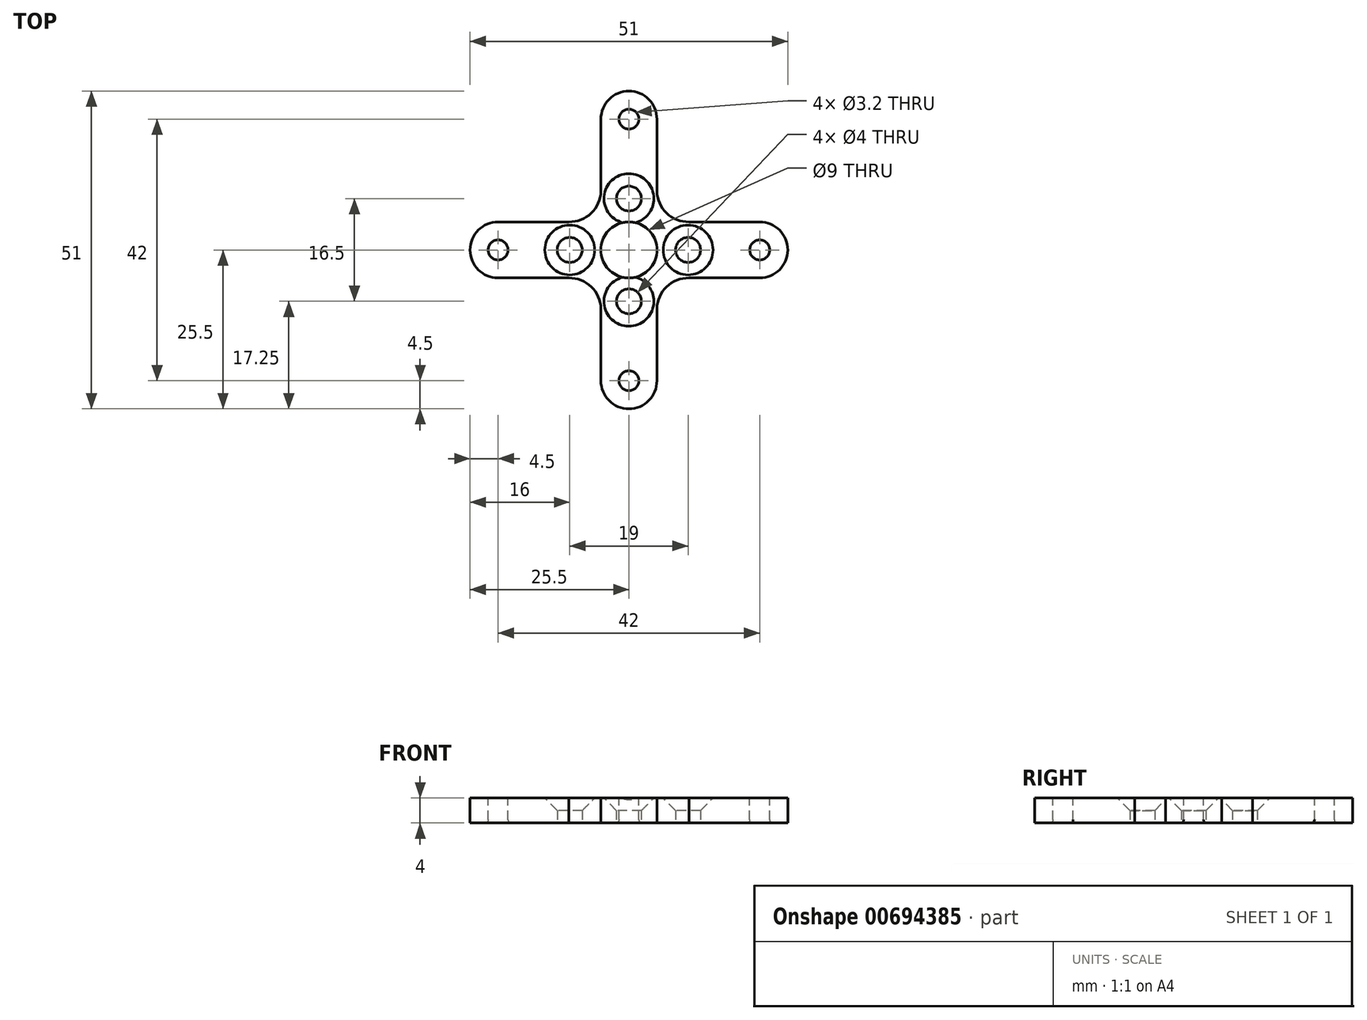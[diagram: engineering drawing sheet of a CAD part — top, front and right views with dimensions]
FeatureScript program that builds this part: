
annotation { "Feature Type Name" : "Feature", "Feature Type Description" : "" }
export const myFeature = defineFeature(function(context is Context, id is Id, definition is map)
    precondition{}
    {
        {
            var Q0;
            Q0=qCreatedBy(makeId("Top.planeOp"),FACE);
            var sketch = newSketch(context, id + "F0", { "sketchPlane" : qUnion([Q0])});
            skLineSegment(sketch, "E0", {"start": v(4.5, -9.46) * mm, "end": v(4.5, -21) * mm});
            skLineSegment(sketch, "E1", {"start": v(9.46, -4.5) * mm, "end": v(21, -4.5) * mm});
            skLineSegment(sketch, "E2.MirrorCS", {"start": v(-4.5, -9.46) * mm, "end": v(-4.5, -21) * mm});
            skLineSegment(sketch, "E3.MirrorCS", {"start": v(9.46, 4.5) * mm, "end": v(21, 4.5) * mm});
            skLineSegment(sketch, "E4.MirrorCS", {"start": v(4.5, 9.46) * mm, "end": v(4.5, 21) * mm});
            skLineSegment(sketch, "E5.MirrorCS", {"start": v(-4.5, 9.46) * mm, "end": v(-4.5, 21) * mm});
            skLineSegment(sketch, "E6.MirrorCS", {"start": v(-9.46, 4.5) * mm, "end": v(-21, 4.5) * mm});
            skLineSegment(sketch, "E7.MirrorCS", {"start": v(-9.46, -4.5) * mm, "end": v(-21, -4.5) * mm});
            skArc(sketch, "E8", {"start": v(21, 4.5) * mm, "mid": v(25.5, 0) * mm, "end": v(21, -4.5) * mm});
            skArc(sketch, "E9", {"start": v(4.5, -21) * mm, "mid": v(0, -25.5) * mm, "end": v(-4.5, -21) * mm});
            skArc(sketch, "E10", {"start": v(-21, -4.5) * mm, "mid": v(-25.5, 0) * mm, "end": v(-21, 4.5) * mm});
            skArc(sketch, "E11", {"start": v(-4.5, 21) * mm, "mid": v(0, 25.5) * mm, "end": v(4.5, 21) * mm});
            skLineSegment(sketch, "E12", {"start": v(0, 0) * mm, "end": v(39.03, 39.03) * mm, "construction": true});
            skLineSegment(sketch, "E13", {"start": v(0, 0) * mm, "end": v(29.48, -29.48) * mm, "construction": true});
            skArc(sketch, "E14", {"start": v(4.5, 9.46) * mm, "mid": v(6.06, 5.9) * mm, "end": v(9.68, 4.5) * mm});
            skArc(sketch, "E15.MirrorCS", {"start": v(-4.5, 9.46) * mm, "mid": v(-6.06, 5.9) * mm, "end": v(-9.68, 4.5) * mm});
            skArc(sketch, "E16.MirrorCS", {"start": v(4.5, -9.46) * mm, "mid": v(6.06, -5.9) * mm, "end": v(9.68, -4.5) * mm});
            skArc(sketch, "E17.MirrorCS", {"start": v(-4.5, -9.46) * mm, "mid": v(-6.06, -5.9) * mm, "end": v(-9.68, -4.5) * mm});
            skSolve(sketch);
        }
        {
            var Q0;
            Q0=makeQuery(id+"F0.imprint","IMPRINT",FACE,{"disambiguationData":[TD([[makeQuery(id+"F0.imprint","IMPRINT",EDGE,{"derivedFrom":sQuery(id+"F0.wireOp",EDGE,"E0")}),-1.0]])]});
            extrude(context, id + "F1", {"entities" : qUnion([Q0]), "depth" : 4 * mm, "offsetDistance" : 25 * mm});
        }
        {
            var Q0;
            Q0=makeQuery(id+"F1.opExtrude","CAP_FACE",FACE,{"disambiguationData":[OSD([sQuery(id+"F0.wireOp",EDGE,"E0"),sQuery(id+"F0.wireOp",EDGE,"E1"),sQuery(id+"F0.wireOp",EDGE,"E2.MirrorCS"),sQuery(id+"F0.wireOp",EDGE,"E3.MirrorCS"),sQuery(id+"F0.wireOp",EDGE,"E4.MirrorCS"),sQuery(id+"F0.wireOp",EDGE,"E5.MirrorCS"),sQuery(id+"F0.wireOp",EDGE,"E6.MirrorCS"),sQuery(id+"F0.wireOp",EDGE,"E7.MirrorCS"),sQuery(id+"F0.wireOp",EDGE,"E8"),sQuery(id+"F0.wireOp",EDGE,"E9"),sQuery(id+"F0.wireOp",EDGE,"E10"),sQuery(id+"F0.wireOp",EDGE,"E11"),sQuery(id+"F0.wireOp",EDGE,"E14"),sQuery(id+"F0.wireOp",EDGE,"E15.MirrorCS"),sQuery(id+"F0.wireOp",EDGE,"E16.MirrorCS"),sQuery(id+"F0.wireOp",EDGE,"E17.MirrorCS")])],"isStart":false});
            var sketch = newSketch(context, id + "F2", { "sketchPlane" : qUnion([Q0])});
            skCircle(sketch, "E18", {"center": v(0, 0) * mm, "radius": 4.5 * mm});
            skSolve(sketch);
        }
        {
            var Q0;
            Q0 = qSketchRegion(id + "F2", true);
            extrude(context, id + "F3", {"entities" : qUnion([Q0]), "operationType" : NewBodyOperationType.REMOVE, "endBound" : BoundingType.THROUGH_ALL, "oppositeDirection" : true, "depth" : 3 * mm, "offsetDistance" : 25 * mm});
        }
        {
            var Q0;
            Q0=makeQuery(id+"F1.opExtrude","CAP_FACE",FACE,{"disambiguationData":[OSD([sQuery(id+"F0.wireOp",EDGE,"E0"),sQuery(id+"F0.wireOp",EDGE,"E1"),sQuery(id+"F0.wireOp",EDGE,"E2.MirrorCS"),sQuery(id+"F0.wireOp",EDGE,"E3.MirrorCS"),sQuery(id+"F0.wireOp",EDGE,"E4.MirrorCS"),sQuery(id+"F0.wireOp",EDGE,"E5.MirrorCS"),sQuery(id+"F0.wireOp",EDGE,"E6.MirrorCS"),sQuery(id+"F0.wireOp",EDGE,"E7.MirrorCS"),sQuery(id+"F0.wireOp",EDGE,"E8"),sQuery(id+"F0.wireOp",EDGE,"E9"),sQuery(id+"F0.wireOp",EDGE,"E10"),sQuery(id+"F0.wireOp",EDGE,"E11"),sQuery(id+"F0.wireOp",EDGE,"E14"),sQuery(id+"F0.wireOp",EDGE,"E15.MirrorCS"),sQuery(id+"F0.wireOp",EDGE,"E16.MirrorCS"),sQuery(id+"F0.wireOp",EDGE,"E17.MirrorCS")])],"isStart":false});
            var sketch = newSketch(context, id + "F4", { "sketchPlane" : qUnion([Q0])});
            skCircle(sketch, "E19", {"center": v(21, 0) * mm, "radius": 1.6 * mm});
            skCircle(sketch, "E20", {"center": v(0, -21) * mm, "radius": 1.6 * mm});
            skCircle(sketch, "E21.MirrorC", {"center": v(-21, 0) * mm, "radius": 1.6 * mm});
            skCircle(sketch, "E22.MirrorC", {"center": v(0, 21) * mm, "radius": 1.6 * mm});
            skSolve(sketch);
        }
        {
            var Q0;
            Q0 = qSketchRegion(id + "F4", true);
            extrude(context, id + "F5", {"entities" : qUnion([Q0]), "operationType" : NewBodyOperationType.REMOVE, "endBound" : BoundingType.THROUGH_ALL, "oppositeDirection" : true, "depth" : 25 * mm, "offsetDistance" : 25 * mm});
        }
        {
            var Q0;
            Q0=qCreatedBy(makeId("Top.planeOp"),FACE);
            var sketch = newSketch(context, id + "F6", { "sketchPlane" : qUnion([Q0])});
            skCircle(sketch, "E23", {"center": v(9.5, 0) * mm, "radius": 2 * mm});
            skCircle(sketch, "E24.MirrorC", {"center": v(-9.5, 0) * mm, "radius": 2 * mm});
            skCircle(sketch, "E25", {"center": v(0, -8.25) * mm, "radius": 2 * mm});
            skCircle(sketch, "E26.MirrorC", {"center": v(0, 8.25) * mm, "radius": 2 * mm});
            skSolve(sketch);
        }
        {
            var Q0;
            Q0 = qSketchRegion(id + "F6", true);
            extrude(context, id + "F7", {"entities" : qUnion([Q0]), "operationType" : NewBodyOperationType.REMOVE, "endBound" : BoundingType.THROUGH_ALL, "depth" : 25 * mm, "offsetDistance" : 25 * mm});
        }
        {
            var Q0;
            Q0=makeQuery(id+"F3.boolean.opBoolean","COPY",EDGE,{"derivedFrom":makeQuery(id+"F3.opExtrude","CAP_EDGE",EDGE,{"disambiguationData":[OSD([sQuery(id+"F2.wireOp",EDGE,"E18")])],"isStart":true})});
            var Q1;
            Q1=makeQuery(id+"F3.boolean.opBoolean","INTERSECT",EDGE,{"derivedFrom":[makeQuery(id+"F1.opExtrude","CAP_FACE",FACE,{"disambiguationData":[OSD([sQuery(id+"F0.wireOp",EDGE,"E0"),sQuery(id+"F0.wireOp",EDGE,"E1"),sQuery(id+"F0.wireOp",EDGE,"E2.MirrorCS"),sQuery(id+"F0.wireOp",EDGE,"E3.MirrorCS"),sQuery(id+"F0.wireOp",EDGE,"E4.MirrorCS"),sQuery(id+"F0.wireOp",EDGE,"E5.MirrorCS"),sQuery(id+"F0.wireOp",EDGE,"E6.MirrorCS"),sQuery(id+"F0.wireOp",EDGE,"E7.MirrorCS"),sQuery(id+"F0.wireOp",EDGE,"E8"),sQuery(id+"F0.wireOp",EDGE,"E9"),sQuery(id+"F0.wireOp",EDGE,"E10"),sQuery(id+"F0.wireOp",EDGE,"E11"),sQuery(id+"F0.wireOp",EDGE,"E14"),sQuery(id+"F0.wireOp",EDGE,"E15.MirrorCS"),sQuery(id+"F0.wireOp",EDGE,"E16.MirrorCS"),sQuery(id+"F0.wireOp",EDGE,"E17.MirrorCS")])],"isStart":true}),makeQuery(id+"F3.opExtrude","SWEPT_FACE",FACE,{"disambiguationData":[OSD([sQuery(id+"F2.wireOp",EDGE,"E18")])]})]});
            var Q2;
            Q2=makeQuery(id+"F5.boolean.opBoolean","COPY",EDGE,{"derivedFrom":makeQuery(id+"F5.opExtrude","CAP_EDGE",EDGE,{"disambiguationData":[OSD([sQuery(id+"F4.wireOp",EDGE,"E19")])],"isStart":true})});
            var Q3;
            Q3=makeQuery(id+"F5.boolean.opBoolean","COPY",EDGE,{"derivedFrom":makeQuery(id+"F5.opExtrude","CAP_EDGE",EDGE,{"disambiguationData":[OSD([sQuery(id+"F4.wireOp",EDGE,"E21.MirrorC")])],"isStart":true})});
            var Q4;
            Q4=makeQuery(id+"F5.boolean.opBoolean","COPY",EDGE,{"derivedFrom":makeQuery(id+"F5.opExtrude","CAP_EDGE",EDGE,{"disambiguationData":[OSD([sQuery(id+"F4.wireOp",EDGE,"E20")])],"isStart":true})});
            var Q5;
            Q5=makeQuery(id+"F5.boolean.opBoolean","COPY",EDGE,{"derivedFrom":makeQuery(id+"F5.opExtrude","CAP_EDGE",EDGE,{"disambiguationData":[OSD([sQuery(id+"F4.wireOp",EDGE,"E22.MirrorC")])],"isStart":true})});
            var Q6;
            Q6=makeQuery(id+"F5.boolean.opBoolean","INTERSECT",EDGE,{"derivedFrom":[makeQuery(id+"F1.opExtrude","CAP_FACE",FACE,{"disambiguationData":[OSD([sQuery(id+"F0.wireOp",EDGE,"E0"),sQuery(id+"F0.wireOp",EDGE,"E1"),sQuery(id+"F0.wireOp",EDGE,"E2.MirrorCS"),sQuery(id+"F0.wireOp",EDGE,"E3.MirrorCS"),sQuery(id+"F0.wireOp",EDGE,"E4.MirrorCS"),sQuery(id+"F0.wireOp",EDGE,"E5.MirrorCS"),sQuery(id+"F0.wireOp",EDGE,"E6.MirrorCS"),sQuery(id+"F0.wireOp",EDGE,"E7.MirrorCS"),sQuery(id+"F0.wireOp",EDGE,"E8"),sQuery(id+"F0.wireOp",EDGE,"E9"),sQuery(id+"F0.wireOp",EDGE,"E10"),sQuery(id+"F0.wireOp",EDGE,"E11"),sQuery(id+"F0.wireOp",EDGE,"E14"),sQuery(id+"F0.wireOp",EDGE,"E15.MirrorCS"),sQuery(id+"F0.wireOp",EDGE,"E16.MirrorCS"),sQuery(id+"F0.wireOp",EDGE,"E17.MirrorCS")])],"isStart":true}),makeQuery(id+"F5.opExtrude","SWEPT_FACE",FACE,{"disambiguationData":[OSD([sQuery(id+"F4.wireOp",EDGE,"E21.MirrorC")])]})]});
            var Q7;
            Q7=makeQuery(id+"F5.boolean.opBoolean","INTERSECT",EDGE,{"derivedFrom":[makeQuery(id+"F1.opExtrude","CAP_FACE",FACE,{"disambiguationData":[OSD([sQuery(id+"F0.wireOp",EDGE,"E0"),sQuery(id+"F0.wireOp",EDGE,"E1"),sQuery(id+"F0.wireOp",EDGE,"E2.MirrorCS"),sQuery(id+"F0.wireOp",EDGE,"E3.MirrorCS"),sQuery(id+"F0.wireOp",EDGE,"E4.MirrorCS"),sQuery(id+"F0.wireOp",EDGE,"E5.MirrorCS"),sQuery(id+"F0.wireOp",EDGE,"E6.MirrorCS"),sQuery(id+"F0.wireOp",EDGE,"E7.MirrorCS"),sQuery(id+"F0.wireOp",EDGE,"E8"),sQuery(id+"F0.wireOp",EDGE,"E9"),sQuery(id+"F0.wireOp",EDGE,"E10"),sQuery(id+"F0.wireOp",EDGE,"E11"),sQuery(id+"F0.wireOp",EDGE,"E14"),sQuery(id+"F0.wireOp",EDGE,"E15.MirrorCS"),sQuery(id+"F0.wireOp",EDGE,"E16.MirrorCS"),sQuery(id+"F0.wireOp",EDGE,"E17.MirrorCS")])],"isStart":true}),makeQuery(id+"F5.opExtrude","SWEPT_FACE",FACE,{"disambiguationData":[OSD([sQuery(id+"F4.wireOp",EDGE,"E19")])]})]});
            var Q8;
            Q8=makeQuery(id+"F5.boolean.opBoolean","INTERSECT",EDGE,{"derivedFrom":[makeQuery(id+"F1.opExtrude","CAP_FACE",FACE,{"disambiguationData":[OSD([sQuery(id+"F0.wireOp",EDGE,"E0"),sQuery(id+"F0.wireOp",EDGE,"E1"),sQuery(id+"F0.wireOp",EDGE,"E2.MirrorCS"),sQuery(id+"F0.wireOp",EDGE,"E3.MirrorCS"),sQuery(id+"F0.wireOp",EDGE,"E4.MirrorCS"),sQuery(id+"F0.wireOp",EDGE,"E5.MirrorCS"),sQuery(id+"F0.wireOp",EDGE,"E6.MirrorCS"),sQuery(id+"F0.wireOp",EDGE,"E7.MirrorCS"),sQuery(id+"F0.wireOp",EDGE,"E8"),sQuery(id+"F0.wireOp",EDGE,"E9"),sQuery(id+"F0.wireOp",EDGE,"E10"),sQuery(id+"F0.wireOp",EDGE,"E11"),sQuery(id+"F0.wireOp",EDGE,"E14"),sQuery(id+"F0.wireOp",EDGE,"E15.MirrorCS"),sQuery(id+"F0.wireOp",EDGE,"E16.MirrorCS"),sQuery(id+"F0.wireOp",EDGE,"E17.MirrorCS")])],"isStart":true}),makeQuery(id+"F5.opExtrude","SWEPT_FACE",FACE,{"disambiguationData":[OSD([sQuery(id+"F4.wireOp",EDGE,"E22.MirrorC")])]})]});
            var Q9;
            Q9=makeQuery(id+"F5.boolean.opBoolean","INTERSECT",EDGE,{"derivedFrom":[makeQuery(id+"F1.opExtrude","CAP_FACE",FACE,{"disambiguationData":[OSD([sQuery(id+"F0.wireOp",EDGE,"E0"),sQuery(id+"F0.wireOp",EDGE,"E1"),sQuery(id+"F0.wireOp",EDGE,"E2.MirrorCS"),sQuery(id+"F0.wireOp",EDGE,"E3.MirrorCS"),sQuery(id+"F0.wireOp",EDGE,"E4.MirrorCS"),sQuery(id+"F0.wireOp",EDGE,"E5.MirrorCS"),sQuery(id+"F0.wireOp",EDGE,"E6.MirrorCS"),sQuery(id+"F0.wireOp",EDGE,"E7.MirrorCS"),sQuery(id+"F0.wireOp",EDGE,"E8"),sQuery(id+"F0.wireOp",EDGE,"E9"),sQuery(id+"F0.wireOp",EDGE,"E10"),sQuery(id+"F0.wireOp",EDGE,"E11"),sQuery(id+"F0.wireOp",EDGE,"E14"),sQuery(id+"F0.wireOp",EDGE,"E15.MirrorCS"),sQuery(id+"F0.wireOp",EDGE,"E16.MirrorCS"),sQuery(id+"F0.wireOp",EDGE,"E17.MirrorCS")])],"isStart":true}),makeQuery(id+"F5.opExtrude","SWEPT_FACE",FACE,{"disambiguationData":[OSD([sQuery(id+"F4.wireOp",EDGE,"E20")])]})]});
            fillet(context, id + "F8", {"entities" : qUnion([Q0, Q1, Q2, Q3, Q4, Q5, Q6, Q7, Q8, Q9]), "radius" : .5 * mm, "tangentPropagation" : true, "allowEdgeOverflow" : false});
        }
        {
            var Q0;
            Q0=makeQuery(id+"F7.boolean.opBoolean","INTERSECT",EDGE,{"derivedFrom":[makeQuery(id+"F1.opExtrude","CAP_FACE",FACE,{"disambiguationData":[OSD([sQuery(id+"F0.wireOp",EDGE,"E0"),sQuery(id+"F0.wireOp",EDGE,"E1"),sQuery(id+"F0.wireOp",EDGE,"E2.MirrorCS"),sQuery(id+"F0.wireOp",EDGE,"E3.MirrorCS"),sQuery(id+"F0.wireOp",EDGE,"E4.MirrorCS"),sQuery(id+"F0.wireOp",EDGE,"E5.MirrorCS"),sQuery(id+"F0.wireOp",EDGE,"E6.MirrorCS"),sQuery(id+"F0.wireOp",EDGE,"E7.MirrorCS"),sQuery(id+"F0.wireOp",EDGE,"E8"),sQuery(id+"F0.wireOp",EDGE,"E9"),sQuery(id+"F0.wireOp",EDGE,"E10"),sQuery(id+"F0.wireOp",EDGE,"E11"),sQuery(id+"F0.wireOp",EDGE,"E14"),sQuery(id+"F0.wireOp",EDGE,"E15.MirrorCS"),sQuery(id+"F0.wireOp",EDGE,"E16.MirrorCS"),sQuery(id+"F0.wireOp",EDGE,"E17.MirrorCS")])],"isStart":false}),makeQuery(id+"F7.opExtrude","SWEPT_FACE",FACE,{"disambiguationData":[OSD([sQuery(id+"F6.wireOp",EDGE,"E26.MirrorC")])]})]});
            var Q1;
            Q1=makeQuery(id+"F7.boolean.opBoolean","INTERSECT",EDGE,{"derivedFrom":[makeQuery(id+"F1.opExtrude","CAP_FACE",FACE,{"disambiguationData":[OSD([sQuery(id+"F0.wireOp",EDGE,"E0"),sQuery(id+"F0.wireOp",EDGE,"E1"),sQuery(id+"F0.wireOp",EDGE,"E2.MirrorCS"),sQuery(id+"F0.wireOp",EDGE,"E3.MirrorCS"),sQuery(id+"F0.wireOp",EDGE,"E4.MirrorCS"),sQuery(id+"F0.wireOp",EDGE,"E5.MirrorCS"),sQuery(id+"F0.wireOp",EDGE,"E6.MirrorCS"),sQuery(id+"F0.wireOp",EDGE,"E7.MirrorCS"),sQuery(id+"F0.wireOp",EDGE,"E8"),sQuery(id+"F0.wireOp",EDGE,"E9"),sQuery(id+"F0.wireOp",EDGE,"E10"),sQuery(id+"F0.wireOp",EDGE,"E11"),sQuery(id+"F0.wireOp",EDGE,"E14"),sQuery(id+"F0.wireOp",EDGE,"E15.MirrorCS"),sQuery(id+"F0.wireOp",EDGE,"E16.MirrorCS"),sQuery(id+"F0.wireOp",EDGE,"E17.MirrorCS")])],"isStart":false}),makeQuery(id+"F7.opExtrude","SWEPT_FACE",FACE,{"disambiguationData":[OSD([sQuery(id+"F6.wireOp",EDGE,"E23")])]})]});
            var Q2;
            Q2=makeQuery(id+"F7.boolean.opBoolean","INTERSECT",EDGE,{"derivedFrom":[makeQuery(id+"F1.opExtrude","CAP_FACE",FACE,{"disambiguationData":[OSD([sQuery(id+"F0.wireOp",EDGE,"E0"),sQuery(id+"F0.wireOp",EDGE,"E1"),sQuery(id+"F0.wireOp",EDGE,"E2.MirrorCS"),sQuery(id+"F0.wireOp",EDGE,"E3.MirrorCS"),sQuery(id+"F0.wireOp",EDGE,"E4.MirrorCS"),sQuery(id+"F0.wireOp",EDGE,"E5.MirrorCS"),sQuery(id+"F0.wireOp",EDGE,"E6.MirrorCS"),sQuery(id+"F0.wireOp",EDGE,"E7.MirrorCS"),sQuery(id+"F0.wireOp",EDGE,"E8"),sQuery(id+"F0.wireOp",EDGE,"E9"),sQuery(id+"F0.wireOp",EDGE,"E10"),sQuery(id+"F0.wireOp",EDGE,"E11"),sQuery(id+"F0.wireOp",EDGE,"E14"),sQuery(id+"F0.wireOp",EDGE,"E15.MirrorCS"),sQuery(id+"F0.wireOp",EDGE,"E16.MirrorCS"),sQuery(id+"F0.wireOp",EDGE,"E17.MirrorCS")])],"isStart":false}),makeQuery(id+"F7.opExtrude","SWEPT_FACE",FACE,{"disambiguationData":[OSD([sQuery(id+"F6.wireOp",EDGE,"E25")])]})]});
            var Q3;
            Q3=makeQuery(id+"F7.boolean.opBoolean","INTERSECT",EDGE,{"derivedFrom":[makeQuery(id+"F1.opExtrude","CAP_FACE",FACE,{"disambiguationData":[OSD([sQuery(id+"F0.wireOp",EDGE,"E0"),sQuery(id+"F0.wireOp",EDGE,"E1"),sQuery(id+"F0.wireOp",EDGE,"E2.MirrorCS"),sQuery(id+"F0.wireOp",EDGE,"E3.MirrorCS"),sQuery(id+"F0.wireOp",EDGE,"E4.MirrorCS"),sQuery(id+"F0.wireOp",EDGE,"E5.MirrorCS"),sQuery(id+"F0.wireOp",EDGE,"E6.MirrorCS"),sQuery(id+"F0.wireOp",EDGE,"E7.MirrorCS"),sQuery(id+"F0.wireOp",EDGE,"E8"),sQuery(id+"F0.wireOp",EDGE,"E9"),sQuery(id+"F0.wireOp",EDGE,"E10"),sQuery(id+"F0.wireOp",EDGE,"E11"),sQuery(id+"F0.wireOp",EDGE,"E14"),sQuery(id+"F0.wireOp",EDGE,"E15.MirrorCS"),sQuery(id+"F0.wireOp",EDGE,"E16.MirrorCS"),sQuery(id+"F0.wireOp",EDGE,"E17.MirrorCS")])],"isStart":false}),makeQuery(id+"F7.opExtrude","SWEPT_FACE",FACE,{"disambiguationData":[OSD([sQuery(id+"F6.wireOp",EDGE,"E24.MirrorC")])]})]});
            chamfer(context, id + "F9", {"entities" : qUnion([Q0, Q1, Q2, Q3]), "width" : 2 * mm, "tangentPropagation" : true});
        }
    });
